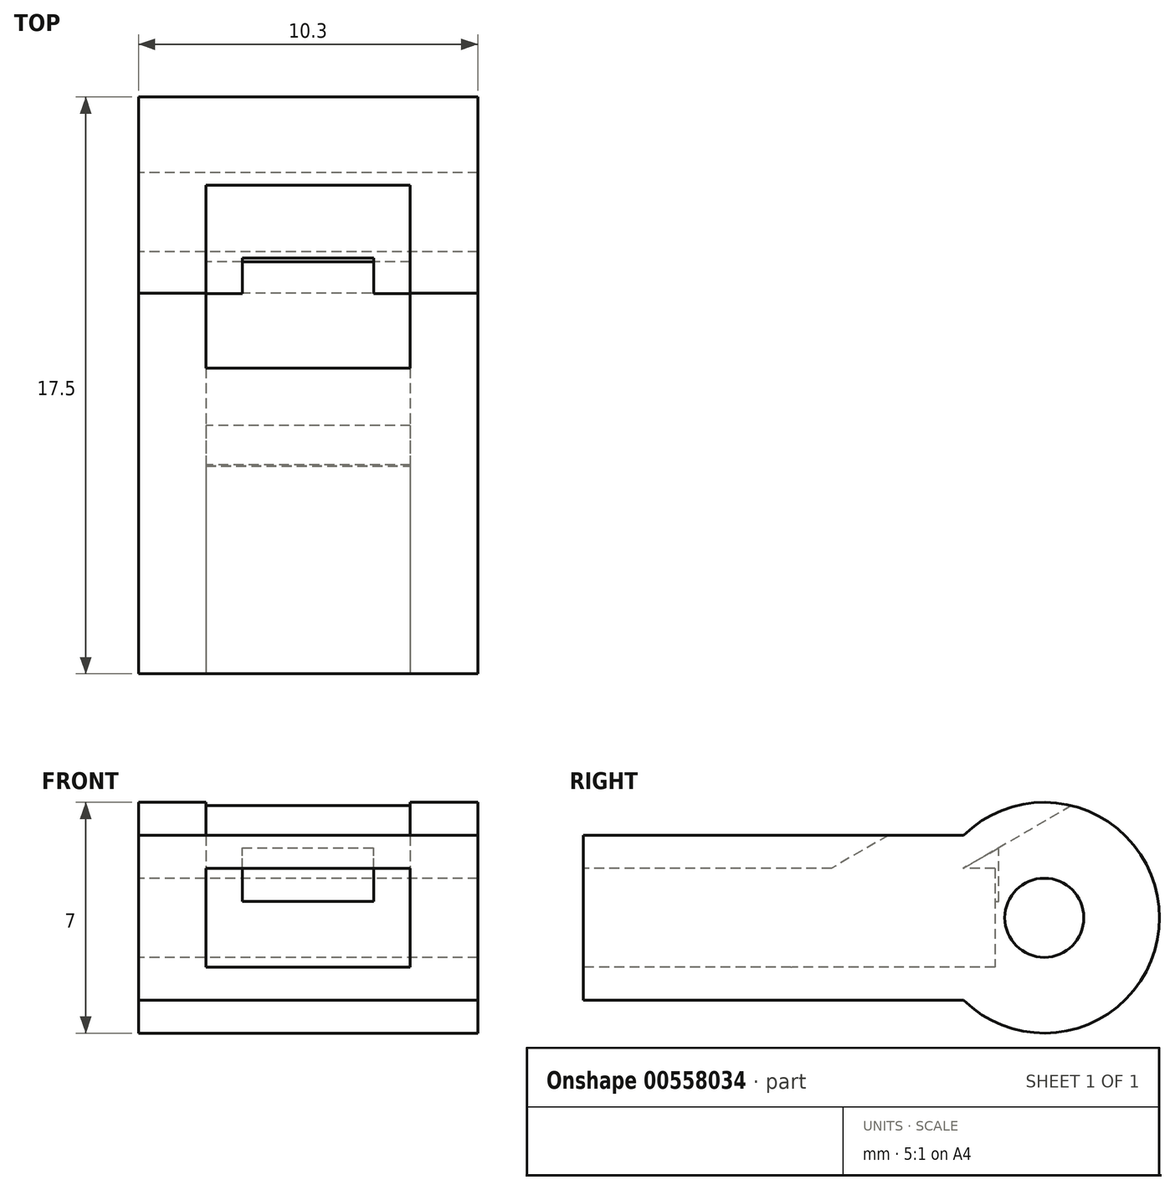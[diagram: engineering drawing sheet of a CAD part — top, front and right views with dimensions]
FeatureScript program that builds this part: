
annotation { "Feature Type Name" : "Feature", "Feature Type Description" : "" }
export const myFeature = defineFeature(function(context is Context, id is Id, definition is map)
    precondition{}
    {
        {
            var Q0;
            Q0=qCreatedBy(makeId("Front.planeOp"),FACE);
            var sketch = newSketch(context, id + "F0", { "sketchPlane" : qUnion([Q0])});
            skPoint(sketch, "E0.middle", {"position": v(0, 0) * mm});
            skLineSegment(sketch, "E1.bottom", {"start": v(5.15, 2.5) * mm, "end": v(-5.15, 2.5) * mm});
            skLineSegment(sketch, "E1.top", {"start": v(5.15, -2.5) * mm, "end": v(-5.15, -2.5) * mm});
            skLineSegment(sketch, "E1.left", {"start": v(5.15, 2.5) * mm, "end": v(5.15, -2.5) * mm});
            skLineSegment(sketch, "E1.right", {"start": v(-5.15, 2.5) * mm, "end": v(-5.15, -2.5) * mm});
            skSolve(sketch);
        }
        {
            var Q0;
            Q0=makeQuery(id+"F0.imprint","IMPRINT",FACE,{"disambiguationData":[TD([[makeQuery(id+"F0.imprint","IMPRINT",EDGE,{"derivedFrom":sQuery(id+"F0.wireOp",EDGE,"E1.bottom")}),1.0]])]});
            extrude(context, id + "F1", {"entities" : qUnion([Q0]), "depth" : 10 * mm, "offsetDistance" : 25 * mm});
        }
        {
            var Q0;
            Q0=makeQuery(id+"F1.opExtrude","SWEPT_FACE",FACE,{"disambiguationData":[OSD([sQuery(id+"F0.wireOp",EDGE,"E1.right")])]});
            var sketch = newSketch(context, id + "F2", { "sketchPlane" : qUnion([Q0])});
            skCircle(sketch, "E2", {"center": v(0, 0) * mm, "radius": 1.2 * mm});
            skCircle(sketch, "E3", {"center": v(0, 0) * mm, "radius": 3.5 * mm});
            skSolve(sketch);
        }
        {
            var Q0;
            {var subQ0=sQuery(id+"F2.wireOp",EDGE,"E2");var subQ1=makeQuery(id+"F1.opExtrude","CAP_EDGE",EDGE,{"disambiguationData":[OSD([sQuery(id+"F0.wireOp",EDGE,"E1.right")])],"isStart":true});var subQ2=makeQuery(id+"F2.imprint","INTERSECT",VERTEX,{"disambiguationData":[OD(0.0)],"derivedFrom":[subQ1,subQ0]});Q0=makeQuery(id+"F2.imprint","IMPRINT",FACE,{"disambiguationData":[TD([[makeQuery(id+"F2.imprint","IMPRINT",EDGE,{"disambiguationData":[TD([[subQ2,-1.0]])],"derivedFrom":subQ0}),-1.0]])]});}
            extrude(context, id + "F3", {"entities" : qUnion([Q0]), "operationType" : NewBodyOperationType.ADD, "oppositeDirection" : true, "depth" : 10.3 * mm, "offsetDistance" : 25 * mm});
        }
        {
            var Q0;
            {var subQ0=sQuery(id+"F2.wireOp",EDGE,"E2");var subQ1=makeQuery(id+"F1.opExtrude","CAP_EDGE",EDGE,{"disambiguationData":[OSD([sQuery(id+"F0.wireOp",EDGE,"E1.right")])],"isStart":true});var subQ2=makeQuery(id+"F2.imprint","INTERSECT",VERTEX,{"disambiguationData":[OD(0.0)],"derivedFrom":[subQ1,subQ0]});Q0=makeQuery(id+"F2.imprint","IMPRINT",FACE,{"disambiguationData":[TD([[makeQuery(id+"F2.imprint","IMPRINT",EDGE,{"disambiguationData":[TD([[subQ2,1.0]])],"derivedFrom":subQ0}),1.0]])]});}
            extrude(context, id + "F4", {"entities" : qUnion([Q0]), "operationType" : NewBodyOperationType.REMOVE, "oppositeDirection" : true, "depth" : 11 * mm, "offsetDistance" : 25 * mm});
        }
        {
            var Q0;
            Q0=makeQuery(id+"F1.opExtrude","SWEPT_FACE",FACE,{"disambiguationData":[OSD([sQuery(id+"F0.wireOp",EDGE,"E1.bottom")])]});
            var sketch = newSketch(context, id + "F5", { "sketchPlane" : qUnion([Q0])});
            skLineSegment(sketch, "E4.bottom", {"start": v(-2, -3.38) * mm, "end": v(2, -3.38) * mm});
            skLineSegment(sketch, "E4.top", {"start": v(-2, -1.38) * mm, "end": v(2, -1.38) * mm});
            skLineSegment(sketch, "E4.left", {"start": v(-2, -3.38) * mm, "end": v(-2, -1.38) * mm});
            skLineSegment(sketch, "E4.right", {"start": v(2, -3.38) * mm, "end": v(2, -1.38) * mm});
            skPoint(sketch, "E4.middle", {"position": v(0, -2.38) * mm});
            skSolve(sketch);
        }
        {
            var Q0;
            Q0 = qSketchRegion(id + "F5", true);
            extrude(context, id + "F6", {"entities" : qUnion([Q0]), "operationType" : NewBodyOperationType.REMOVE, "oppositeDirection" : true, "depth" : 2 * mm, "offsetDistance" : 25 * mm, "hasSecondDirection" : true, "secondDirectionOppositeDirection" : false, "secondDirectionDepth" : 5 * mm});
        }
        {
            var Q0;
            Q0=makeQuery(id+"F1.opExtrude","CAP_FACE",FACE,{"disambiguationData":[OSD([sQuery(id+"F0.wireOp",EDGE,"E1.bottom"),sQuery(id+"F0.wireOp",EDGE,"E1.top"),sQuery(id+"F0.wireOp",EDGE,"E1.left"),sQuery(id+"F0.wireOp",EDGE,"E1.right")])],"isStart":false});
            var sketch = newSketch(context, id + "F7", { "sketchPlane" : qUnion([Q0])});
            skLineSegment(sketch, "E5.bottom", {"start": v(3.1, 1.5) * mm, "end": v(-3.1, 1.5) * mm});
            skLineSegment(sketch, "E5.top", {"start": v(3.1, -1.5) * mm, "end": v(-3.1, -1.5) * mm});
            skLineSegment(sketch, "E5.left", {"start": v(3.1, 1.5) * mm, "end": v(3.1, -1.5) * mm});
            skLineSegment(sketch, "E5.right", {"start": v(-3.1, 1.5) * mm, "end": v(-3.1, -1.5) * mm});
            skPoint(sketch, "E5.middle", {"position": v(0, 0) * mm});
            skSolve(sketch);
        }
        {
            var Q0;
            Q0=makeQuery(id+"F7.imprint","IMPRINT",FACE,{"disambiguationData":[TD([[makeQuery(id+"F7.imprint","IMPRINT",EDGE,{"derivedFrom":sQuery(id+"F7.wireOp",EDGE,"E5.bottom")}),1.0]])]});
            extrude(context, id + "F8", {"entities" : qUnion([Q0]), "operationType" : NewBodyOperationType.REMOVE, "oppositeDirection" : true, "depth" : 8.5 * mm, "offsetDistance" : 25 * mm});
        }
        {
            var Q0;
            Q0=makeQuery(id+"F1.opExtrude","CAP_EDGE",EDGE,{"disambiguationData":[OSD([sQuery(id+"F0.wireOp",EDGE,"E1.bottom")])],"isStart":false});
            cPlane(context, id + "F9", {"entities" : qUnion([Q0]), "cplaneType" : CPlaneType.LINE_ANGLE, "offset" : 25 * mm, "angle" : 30 * degree, "oppositeDirection" : true, "width" : 150 * mm, "height" : 150 * mm});
        }
        {
            var Q0;
            Q0=qCreatedBy(id+"F9.planeOp",FACE);
            var sketch = newSketch(context, id + "F10", { "sketchPlane" : qUnion([Q0])});
            skLineSegment(sketch, "E6.bottom", {"start": v(-3.1, 2.53) * mm, "end": v(3.1, 2.53) * mm});
            skLineSegment(sketch, "E6.top", {"start": v(-3.1, 4.53) * mm, "end": v(3.1, 4.53) * mm});
            skLineSegment(sketch, "E6.left", {"start": v(-3.1, 2.53) * mm, "end": v(-3.1, 4.53) * mm});
            skLineSegment(sketch, "E6.right", {"start": v(3.1, 2.53) * mm, "end": v(3.1, 4.53) * mm});
            skPoint(sketch, "E6.middle", {"position": v(0, 3.53) * mm});
            skSolve(sketch);
        }
        {
            var Q0;
            Q0 = qSketchRegion(id + "F10", true);
            extrude(context, id + "F11", {"entities" : qUnion([Q0]), "operationType" : NewBodyOperationType.REMOVE, "oppositeDirection" : true, "depth" : 25 * mm, "offsetDistance" : 25 * mm});
        }
        {
            var Q0;
            Q0=makeQuery(id+"F7.imprint","IMPRINT",FACE,{"disambiguationData":[TD([[makeQuery(id+"F7.imprint","IMPRINT",EDGE,{"derivedFrom":sQuery(id+"F7.wireOp",EDGE,"E5.bottom")}),-1.0]])]});
            extrude(context, id + "F12", {"entities" : qUnion([Q0]), "operationType" : NewBodyOperationType.ADD, "depth" : 4 * mm, "offsetDistance" : 25 * mm});
        }
    });
